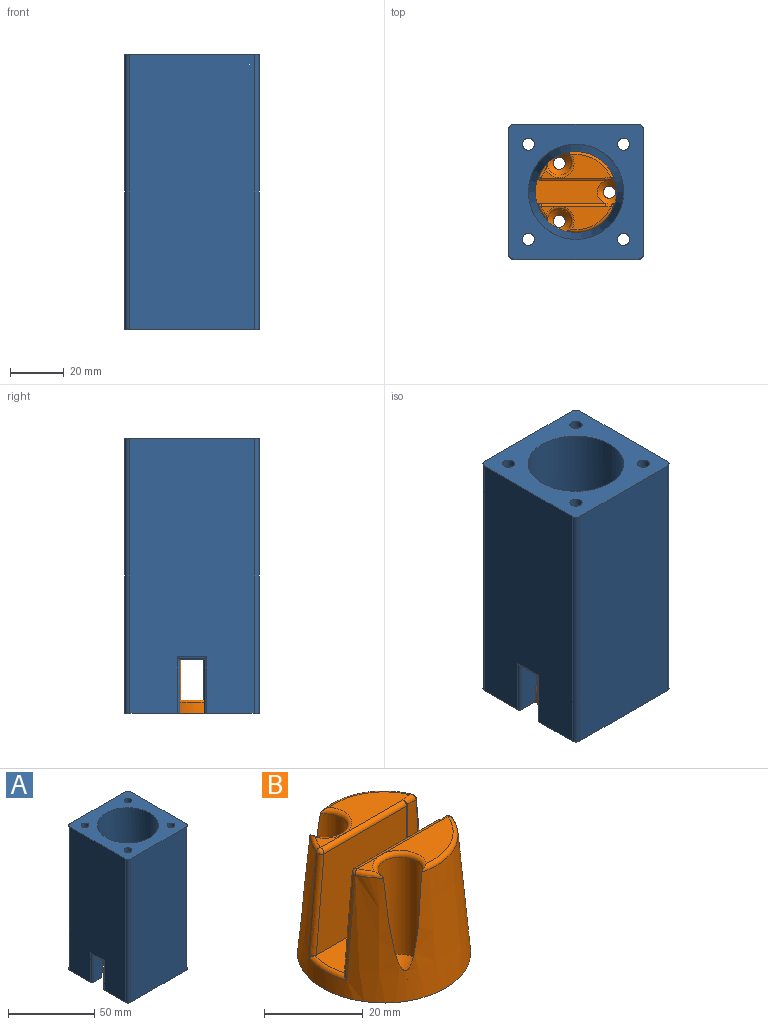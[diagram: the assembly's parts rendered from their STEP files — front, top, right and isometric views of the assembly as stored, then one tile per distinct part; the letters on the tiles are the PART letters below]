
ASSEMBLY  parts=2 mates=1
PART A: 38 faces, bbox 50x50x102 mm
  f0: plane 102x46mm, normal (-1,0,0), area 4461.8mm2, adj f2,f6,f18,f19,f25,f32,f33,f34
  f1: cone r=17.71mm half-angle=5deg, axis (0,0,-1), area 2737.8mm2, adj f2,f24,f25,f26,f27,f28,f29,f30
  f2: plane 50x20.52mm, normal (0,0,-1), area 562mm2, adj f0,f1,f3,f4,f16,f19,f20,f21
  f3: plane 102x46mm, normal (0,-1,0), area 4692mm2, adj f2,f6,f16,f19
  f4: plane 102x46mm, normal (1,0,0), area 4461.8mm2, adj f2,f6,f16,f17,f25,f35,f36,f37
  f5: plane 102x46mm, normal (0,1,0), area 4692mm2, adj f6,f17,f18,f25
  f6: plane 50x50mm, normal (0,0,1), area 1447.5mm2, adj f0,f3,f4,f5,f7,f9,f11,f13
  f7: cylinder r=2.25mm len=4.5mm, axis (0,0,-1), area 39.2mm2, adj f6,f8
  f8: cone r=2.25mm half-angle=45deg, axis (0,0,-1), area 66.7mm2, adj f7,f20
  f9: cylinder r=2.25mm len=4.5mm, axis (0,0,-1), area 39.2mm2, adj f6,f10
  f10: cone r=2.25mm half-angle=45deg, axis (0,0,-1), area 66.7mm2, adj f9,f21
  f11: cylinder r=2.25mm len=4.5mm, axis (0,0,-1), area 39.2mm2, adj f6,f12
  f12: cone r=2.25mm half-angle=45deg, axis (0,0,-1), area 66.7mm2, adj f11,f22
  f13: cylinder r=2.25mm len=4.5mm, axis (0,0,-1), area 39.2mm2, adj f6,f14
  f14: cone r=2.25mm half-angle=45deg, axis (0,0,-1), area 66.7mm2, adj f13,f23
  f15: cylinder r=17.71mm len=42mm, axis (0,0,-1), area 4673.8mm2, adj f6,f24
  f16: cylinder r=2mm len=102mm, axis (0,0,1), area 320.4mm2, adj f2,f3,f4,f6
  f17: cylinder r=2mm len=102mm, axis (0,0,-1), area 320.4mm2, adj f4,f5,f6,f25
  f18: cylinder r=2mm len=102mm, axis (0,0,1), area 320.4mm2, adj f0,f5,f6,f25
  f19: cylinder r=2mm len=102mm, axis (0,0,-1), area 320.4mm2, adj f0,f2,f3,f6
  f20: cylinder r=4.48mm len=97mm, axis (0,0,1), area 2730.4mm2, adj f2,f8
  f21: cylinder r=4.48mm len=97mm, axis (0,0,1), area 2730.4mm2, adj f2,f10
  f22: cylinder r=4.48mm len=97mm, axis (0,0,1), area 2730.4mm2, adj f12,f25
  f23: cylinder r=4.48mm len=97mm, axis (0,0,1), area 2730.4mm2, adj f14,f25
  f24: cone r=17.71mm half-angle=5deg, axis (0,0,1), area 3102.9mm2, adj f1,f15
  f25: plane 50x20.51mm, normal (0,0,-1), area 561.9mm2, adj f0,f1,f4,f5,f17,f18,f22,f23
  f26: plane 8.96x8.68mm, normal (0,0,-1), area 74mm2, adj f1,f27,f28,f33
  f27: plane 20.03x8.71mm, normal (0,-1,0), area 155.5mm2, adj f1,f25,f26,f32
  f28: plane 20.03x8.71mm, normal (0,1,0), area 155.4mm2, adj f1,f2,f26,f34
  f29: plane 8.96x8.68mm, normal (0,0,-1), area 74mm2, adj f1,f30,f31,f36
  f30: plane 20.03x8.71mm, normal (0,1,0), area 155.4mm2, adj f1,f2,f29,f35
  f31: plane 20.03x8.71mm, normal (0,-1,0), area 155.5mm2, adj f1,f25,f29,f37
  f32: cylinder r=1mm len=21mm, axis (0,0,1), area 32mm2, adj f0,f25,f27,f33
  f33: cylinder r=1mm len=10.96mm, axis (0,1,0), area 15.2mm2, adj f0,f26,f32,f34
  f34: cylinder r=1mm len=21mm, axis (0,0,-1), area 32mm2, adj f0,f2,f28,f33
  f35: cylinder r=1mm len=21mm, axis (0,0,1), area 32mm2, adj f2,f4,f30,f36
  f36: cylinder r=1mm len=10.96mm, axis (0,-1,0), area 15.2mm2, adj f4,f29,f35,f37
  f37: cylinder r=1mm len=21mm, axis (0,0,-1), area 32mm2, adj f4,f25,f31,f36
PART B: 45 faces, bbox 37.2x35x39.2 mm
  f0: plane 2.1x1.55mm, normal (0,0,1), area 1mm2, adj f18,f24,f42,f43
  f1: cone r=17.51mm half-angle=5deg, axis (0,0,-1), area 2158.3mm2, adj f4,f5,f9,f10,f13,f19,f20,f21
  f2: plane 25.81x8.72mm, normal (0,0,1), area 102.8mm2, adj f5,f7,f19,f21,f37
  f3: cylinder r=4.48mm len=24mm, axis (0,0,-1), area 64.4mm2, adj f7,f18,f24,f39,f43
  f4: torus R=13.97mm, axis (0,0,1), area 7.2mm2, adj f1,f8,f20,f32
  f5: torus R=13.97mm, axis (0,0,1), area 30mm2, adj f1,f2,f7,f21,f44
  f6: torus R=5.48mm, axis (0,0,1), area 4.2mm2, adj f8,f16,f22,f30,f40,f41
  f7: torus R=5.48mm, axis (0,0,1), area 3.7mm2, adj f2,f3,f5,f38,f43,f44
  f8: plane 25.84x8.81mm, normal (0,0,1), area 104.8mm2, adj f4,f6,f20,f22,f31
  f9: plane 35.02x35.02mm, normal (0,0,-1), area 915.6mm2, adj f1,f11,f14,f17
  f10: cylinder r=4.48mm len=24mm, axis (0,0,-1), area 533.6mm2, adj f1,f12,f20
  f11: cylinder r=2.25mm len=4.5mm, axis (0,0,1), area 39.2mm2, adj f9,f12
  f12: cone r=2.25mm half-angle=45deg, axis (0,0,1), area 66.7mm2, adj f10,f11
  f13: cylinder r=4.48mm len=24mm, axis (0,0,-1), area 534.7mm2, adj f1,f15,f21
  f14: cylinder r=2.25mm len=4.5mm, axis (0,0,1), area 39.2mm2, adj f9,f15
  f15: cone r=2.25mm half-angle=45deg, axis (0,0,1), area 66.7mm2, adj f13,f14
  f16: cylinder r=4.48mm len=24mm, axis (0,0,-1), area 74.2mm2, adj f6,f18,f23,f29,f41
  f17: cylinder r=2.25mm len=4.5mm, axis (0,0,1), area 39.2mm2, adj f9,f18
  f18: cone r=2.25mm half-angle=45deg, axis (0,0,1), area 66mm2, adj f0,f3,f16,f17,f25,f26,f42
  f19: torus R=13.97mm, axis (0,0,1), area 7.1mm2, adj f1,f2,f21,f36
  f20: torus R=5.48mm, axis (0,0,1), area 28.6mm2, adj f1,f4,f8,f10,f22
  f21: torus R=5.48mm, axis (0,0,1), area 28.6mm2, adj f1,f2,f5,f13,f19
  f22: torus R=13.97mm, axis (0,0,1), area 29.8mm2, adj f1,f6,f8,f20,f40
  f23: plane 12.5x1.16mm, normal (0,-1,0), area 7.3mm2, adj f16,f25,f41
  f24: plane 14.57x1.36mm, normal (0,1,0), area 9.9mm2, adj f0,f3,f43
  f25: plane 1.87x1.47mm, normal (0,0,1), area 0.9mm2, adj f18,f23,f41,f42
  f26: plane 27.28x8.57mm, normal (0,0,1), area 207.7mm2, adj f18,f27,f28,f29,f33,f34,f35,f39
  f27: plane 26.01x24mm, normal (0,1,0), area 597.4mm2, adj f26,f35,f37,f39
  f28: plane 25.79x24mm, normal (0,-1,0), area 592.1mm2, adj f26,f29,f31,f33
  f29: cylinder r=1mm len=24mm, axis (0,0,-1), area 8.2mm2, adj f16,f26,f28,f30
  f30: sphere r=1mm, area 0.3mm2, adj f6,f29,f31
  f31: cylinder r=1mm len=23.55mm, axis (1,0,0), area 37mm2, adj f8,f28,f30,f32
  f32: sphere r=1mm, area 1.2mm2, adj f4,f31,f33
  f33: bspline ~39.23x5mm, area 47.1mm2, adj f1,f26,f28,f32,f34
  f34: torus R=16.16mm, axis (0,0,1), area 14.8mm2, adj f1,f26,f33,f35
  f35: bspline ~39.23x5.01mm, area 47.2mm2, adj f1,f26,f27,f34,f36
  f36: sphere r=1mm, area 1.2mm2, adj f19,f35,f37
  f37: cylinder r=1mm len=23.77mm, axis (-1,0,0), area 37.3mm2, adj f2,f27,f36,f38
  f38: sphere r=1mm, area 0.3mm2, adj f7,f37,f39
  f39: cylinder r=1mm len=24mm, axis (0,0,-1), area 7mm2, adj f3,f26,f27,f38
  f40: sphere r=1mm, area 0.8mm2, adj f6,f22,f41
  f41: bspline ~39.23x5mm, area 42.9mm2, adj f1,f6,f16,f23,f25,f40,f42
  f42: torus R=16.16mm, axis (0,0,1), area 13.2mm2, adj f0,f1,f18,f25,f41,f43
  f43: bspline ~39.23x5.01mm, area 44.4mm2, adj f0,f1,f3,f7,f24,f42,f44
  f44: sphere r=1mm, area 0.9mm2, adj f5,f7,f43
PLACE A at identity
PLACE B t=(0,0,-97)mm
MATE revolute B.f1 <-> A.f1  axis (0,0,-1) through (0,0,-97)mm
